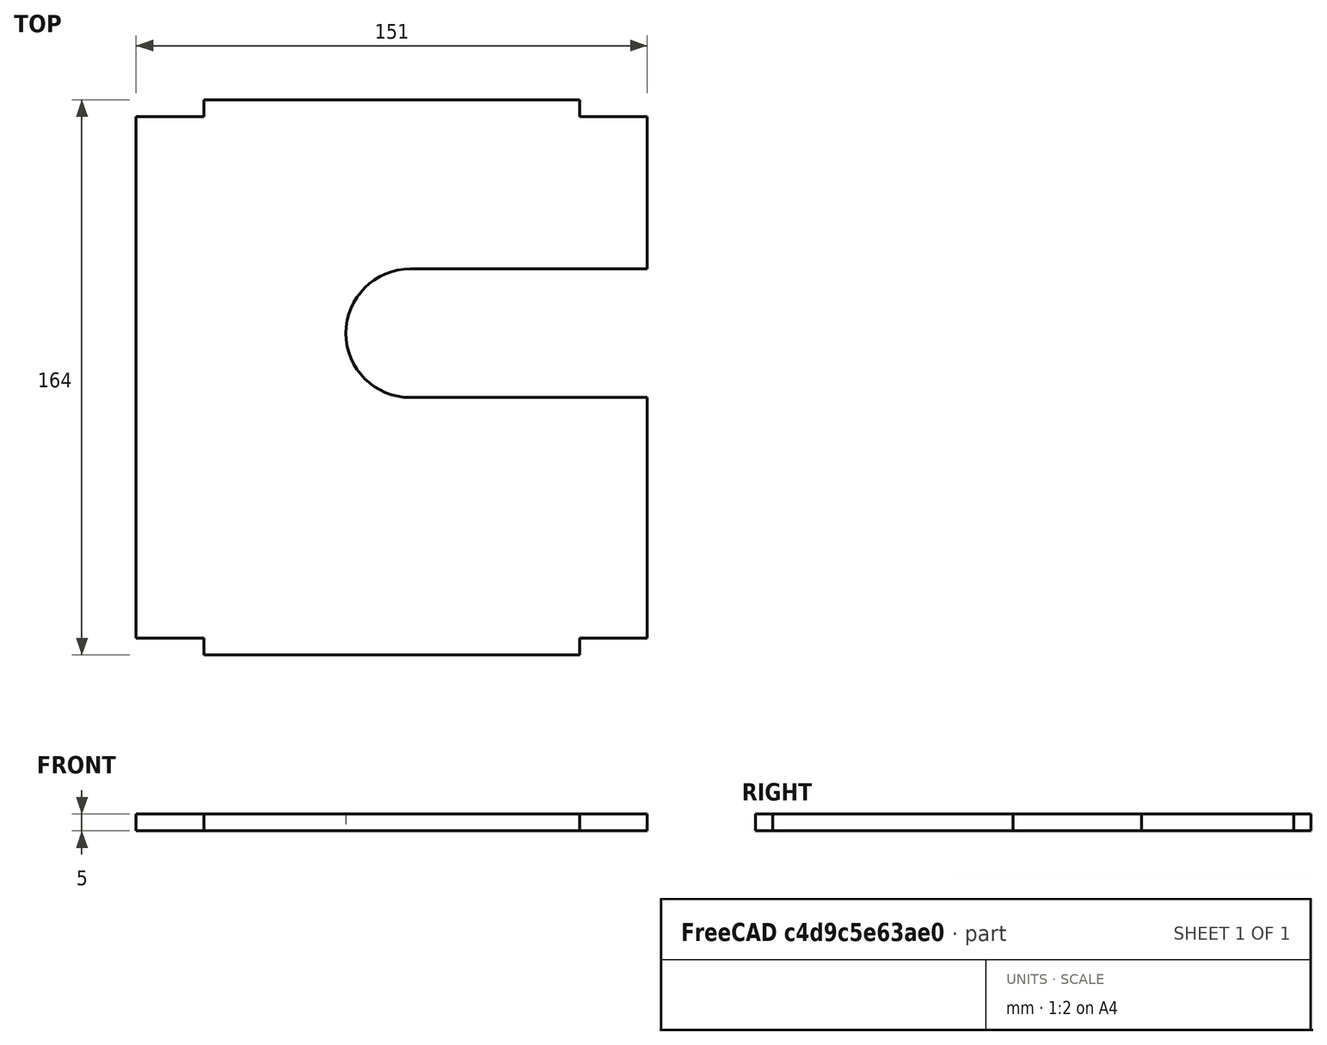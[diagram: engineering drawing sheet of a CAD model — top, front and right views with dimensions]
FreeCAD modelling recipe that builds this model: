
FCSTD DOCUMENT  (FreeCAD 0.15R4671 (Git))
Label: upper_side_axis_A
License: All rights reserved
LicenseURL: http://en.wikipedia.org/wiki/All_rights_reserved
objects: Sketcher::SketchObject×1, PartDesign::Pad×1
note: 3 computed .brp shape members not serialized (recipe doc carries the construction recipe); baked Part::Feature solids carry a one-line shape summary decoded from their .brp

FEATURE [Sketcher::SketchObject] Sketch
  sketch-geometry (16):
    g0: LineSegment StartX=-55.5 StartY=82 StartZ=0 EndX=-55.5 EndY=77 EndZ=0
    g1: LineSegment StartX=-55.5 StartY=77 StartZ=0 EndX=-75.5 EndY=77 EndZ=0
    g2: LineSegment StartX=-75.5 StartY=77 StartZ=0 EndX=-75.5 EndY=-77 EndZ=0
    g3: LineSegment StartX=-75.5 StartY=-77 StartZ=0 EndX=-55.5 EndY=-77 EndZ=0
    g4: LineSegment StartX=-55.5 StartY=-77 StartZ=0 EndX=-55.5 EndY=-82 EndZ=0
    g5: LineSegment StartX=-55.5 StartY=-82 StartZ=0 EndX=55.5 EndY=-82 EndZ=0
    g6: LineSegment StartX=55.5 StartY=-82 StartZ=0 EndX=55.5 EndY=-77 EndZ=0
    g7: LineSegment StartX=55.5 StartY=-77 StartZ=0 EndX=75.5 EndY=-77 EndZ=0
    g8: LineSegment StartX=75.5 StartY=-77 StartZ=0 EndX=75.5 EndY=-6 EndZ=0
    g9: LineSegment StartX=75.5 StartY=-6 StartZ=0 EndX=5.5 EndY=-6 EndZ=0
    g10: ArcOfCircle CenterX=5.5 CenterY=13 CenterZ=0 NormalX=0 NormalY=0 NormalZ=1 Radius=19 StartAngle=1.5708 EndAngle=4.71239
    g11: LineSegment StartX=5.5 StartY=32 StartZ=0 EndX=75.5 EndY=32 EndZ=0
    g12: LineSegment StartX=75.5 StartY=32 StartZ=0 EndX=75.5 EndY=77 EndZ=0
    g13: LineSegment StartX=75.5 StartY=77 StartZ=0 EndX=55.5 EndY=77 EndZ=0
    g14: LineSegment StartX=55.5 StartY=77 StartZ=0 EndX=55.5 EndY=82 EndZ=0
    g15: LineSegment StartX=55.5 StartY=82 StartZ=0 EndX=-55.5 EndY=82 EndZ=0
  constraints (49):
    c: Radius(g10) = 19
    c: Coincident(g1,g2)
    c: Coincident(g0,g1)
    c: Coincident(g0,g15)
    c: Coincident(g14,g15)
    c: Coincident(g13,g14)
    c: Coincident(g12,g13)
    c: Coincident(g11,g12)
    c: Coincident(g10,g11)
    c: Coincident(g9,g10)
    c: Coincident(g8,g9)
    c: Coincident(g7,g8)
    c: Coincident(g6,g7)
    c: Coincident(g5,g6)
    c: Coincident(g4,g5)
    c: Coincident(g3,g4)
    c: Coincident(g2,g3)
    c: Vertical(g2)
    c: Vertical(g4)
    c: Vertical(g0)
    c: Vertical(g14)
    c: Vertical(g6)
    c: Vertical(g8)
    c: Vertical(g12)
    c: Horizontal(g1)
    c: Horizontal(g15)
    c: Horizontal(g13)
    c: Horizontal(g11)
    c: Horizontal(g9)
    c: Horizontal(g7)
    c: Horizontal(g5)
    c: Horizontal(g3)
    c: DistanceY(g14) = 5
    c: Equal(g14,g0)
    c: Equal(g0,g4)
    c: Equal(g4,g6)
    c: DistanceX(g11) = 70
    c: Tangent(g12,g8)
    c: Tangent(g14,g6)
    c: Tangent(g4,g0)
    c: Equal(g1,g13)
    c: DistanceX(g15) = -111
    c: DistanceX(g1,g12) = 151
    c: DistanceY(g2) = -154
    c: Equal(g9,g11)
    c: DistanceY(g12) = 45
    c: DistanceX(g10,g11) = 70
    c: Symmetric(g1,g2,g-1)
    c: Symmetric(g7,g2,g-2)
FEATURE [PartDesign::Pad] Pad
  Length = 5
  Length2 = 100
  Midplane = true
  Sketch = -> Sketch
  Type = 0
